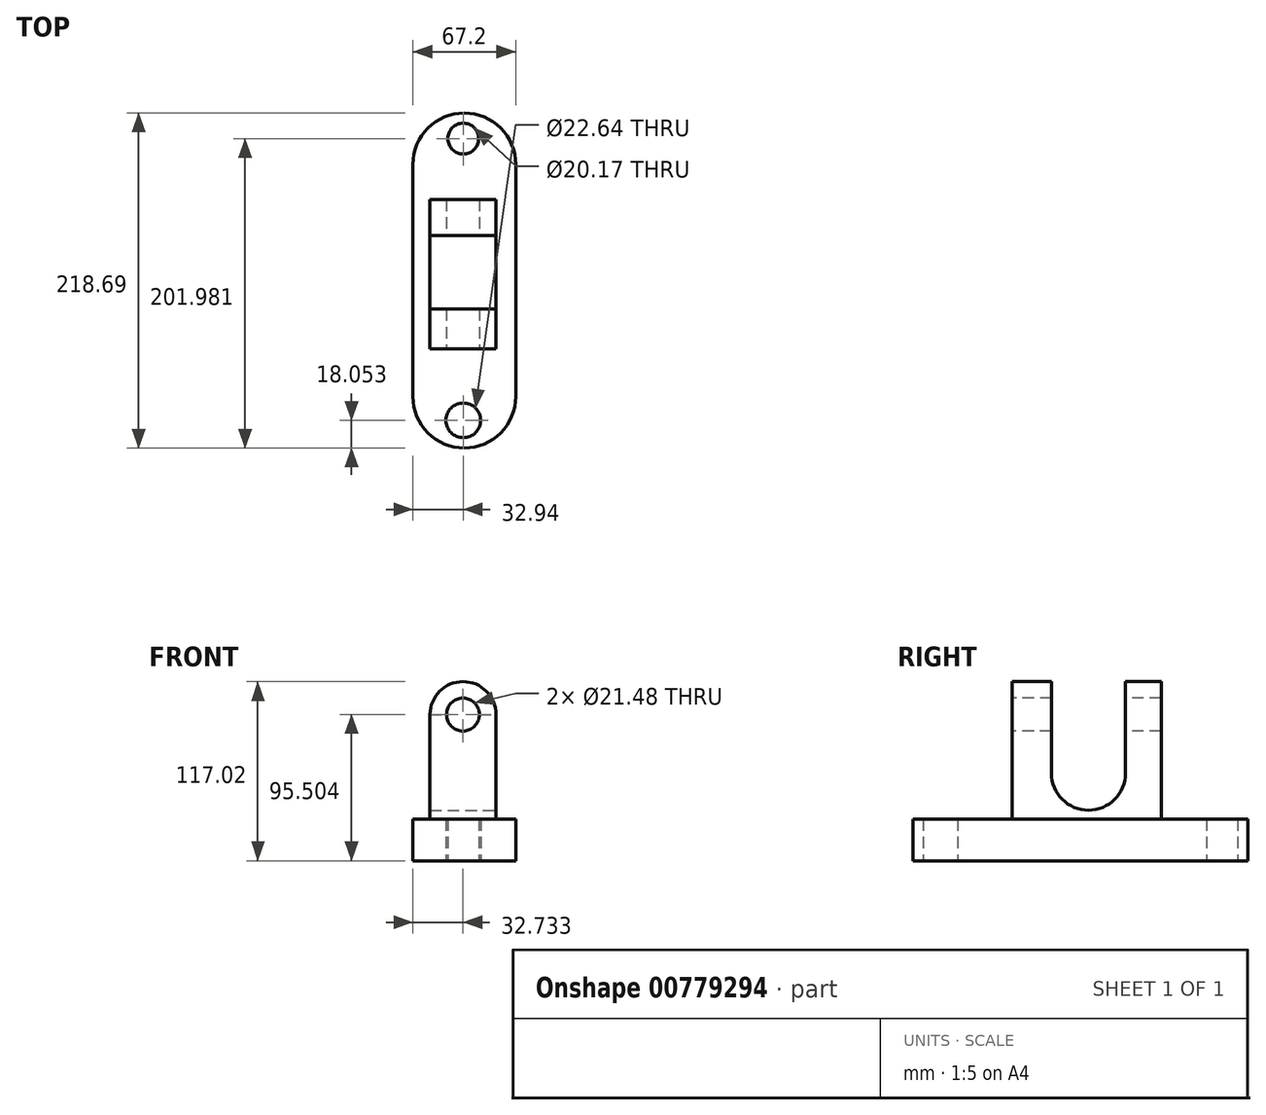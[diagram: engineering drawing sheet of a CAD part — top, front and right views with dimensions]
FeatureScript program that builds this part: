
annotation { "Feature Type Name" : "Feature", "Feature Type Description" : "" }
export const myFeature = defineFeature(function(context is Context, id is Id, definition is map)
    precondition{}
    {
        {
            var Q0;
            Q0=qCreatedBy(makeId("Top.planeOp"),FACE);
            var sketch = newSketch(context, id + "F0", { "sketchPlane" : qUnion([Q0])});
            skLineSegment(sketch, "E0.bottom", {"start": v(-32.94, -75.57) * mm, "end": v(34.26, -75.57) * mm});
            skLineSegment(sketch, "E0.top", {"start": v(-32.94, 75.92) * mm, "end": v(34.26, 75.92) * mm});
            skLineSegment(sketch, "E0.left", {"start": v(-32.94, -75.57) * mm, "end": v(-32.94, 75.92) * mm});
            skLineSegment(sketch, "E0.right", {"start": v(34.26, -75.57) * mm, "end": v(34.26, 75.92) * mm});
            skArc(sketch, "E1", {"start": v(-32.94, -75.57) * mm, "mid": v(0.66, -109.17) * mm, "end": v(34.26, -75.57) * mm});
            skArc(sketch, "E2", {"start": v(34.26, 75.92) * mm, "mid": v(0.66, 109.52) * mm, "end": v(-32.94, 75.92) * mm});
            skCircle(sketch, "E3", {"center": v(0, -91.12) * mm, "radius": 11.32 * mm});
            skCircle(sketch, "E4", {"center": v(0, 92.81) * mm, "radius": 10.08 * mm});
            skSolve(sketch);
        }
        {
            var Q0;
            Q0=makeQuery(id+"F0.imprint","IMPRINT",FACE,{"disambiguationData":[TD([[makeQuery(id+"F0.imprint","IMPRINT",EDGE,{"derivedFrom":sQuery(id+"F0.wireOp",EDGE,"E0.bottom")}),1.0]])]});
            var Q1;
            Q1=makeQuery(id+"F0.imprint","IMPRINT",FACE,{"disambiguationData":[TD([[makeQuery(id+"F0.imprint","IMPRINT",EDGE,{"derivedFrom":sQuery(id+"F0.wireOp",EDGE,"E0.top")}),1.0]])]});
            var Q2;
            Q2=makeQuery(id+"F0.imprint","IMPRINT",FACE,{"disambiguationData":[TD([[makeQuery(id+"F0.imprint","IMPRINT",EDGE,{"derivedFrom":sQuery(id+"F0.wireOp",EDGE,"E0.bottom")}),-1.0]])]});
            extrude(context, id + "F1", {"entities" : qUnion([Q0, Q1, Q2]), "depth" : 27.18 * mm, "offsetDistance" : 25.4 * mm});
        }
        {
            var Q0;
            Q0=makeQuery(id+"F1.opExtrude","CAP_FACE",FACE,{"disambiguationData":[OSD([sQuery(id+"F0.wireOp",EDGE,"E0.left"),sQuery(id+"F0.wireOp",EDGE,"E0.right"),sQuery(id+"F0.wireOp",EDGE,"E1"),sQuery(id+"F0.wireOp",EDGE,"E2"),sQuery(id+"F0.wireOp",EDGE,"E3"),sQuery(id+"F0.wireOp",EDGE,"E4")])],"isStart":false});
            var sketch = newSketch(context, id + "F2", { "sketchPlane" : qUnion([Q0])});
            skLineSegment(sketch, "E5.bottom", {"start": v(-21.73, -44.46) * mm, "end": v(21.31, -44.46) * mm});
            skLineSegment(sketch, "E5.top", {"start": v(-21.73, 53.01) * mm, "end": v(21.31, 53.01) * mm});
            skLineSegment(sketch, "E5.left", {"start": v(-21.73, -44.46) * mm, "end": v(-21.73, 53.01) * mm});
            skLineSegment(sketch, "E5.right", {"start": v(21.31, -44.46) * mm, "end": v(21.31, 53.01) * mm});
            skSolve(sketch);
        }
        {
            var Q0;
            Q0 = qSketchRegion(id + "F2", true);
            extrude(context, id + "F3", {"entities" : qUnion([Q0]), "operationType" : NewBodyOperationType.ADD, "depth" : 68.33 * mm, "offsetDistance" : 25.4 * mm});
        }
        {
            var Q0;
            Q0=makeQuery(id+"F3.opExtrude","SWEPT_FACE",FACE,{"disambiguationData":[OSD([sQuery(id+"F2.wireOp",EDGE,"E5.right")])]});
            var sketch = newSketch(context, id + "F4", { "sketchPlane" : qUnion([Q0])});
            skLineSegment(sketch, "E6.bottom", {"start": v(-18.68, 95.5) * mm, "end": v(29.7, 95.5) * mm});
            skLineSegment(sketch, "E6.top", {"start": v(-18.68, 57.26) * mm, "end": v(29.7, 57.26) * mm});
            skLineSegment(sketch, "E6.left", {"start": v(-18.68, 95.5) * mm, "end": v(-18.68, 57.26) * mm});
            skLineSegment(sketch, "E6.right", {"start": v(29.7, 95.5) * mm, "end": v(29.7, 57.26) * mm});
            skArc(sketch, "E7", {"start": v(-18.68, 57.26) * mm, "mid": v(5.51, 33.07) * mm, "end": v(29.7, 57.26) * mm});
            skSolve(sketch);
        }
        {
            var Q0;
            Q0=makeQuery(id+"F4.imprint","IMPRINT",FACE,{"disambiguationData":[TD([[makeQuery(id+"F4.imprint","IMPRINT",EDGE,{"derivedFrom":sQuery(id+"F4.wireOp",EDGE,"E6.bottom")}),-1.0]])]});
            var Q1;
            Q1=makeQuery(id+"F4.imprint","IMPRINT",FACE,{"disambiguationData":[TD([[makeQuery(id+"F4.imprint","IMPRINT",EDGE,{"derivedFrom":sQuery(id+"F4.wireOp",EDGE,"E6.top")}),-1.0]])]});
            extrude(context, id + "F5", {"entities" : qUnion([Q0, Q1]), "operationType" : NewBodyOperationType.REMOVE, "oppositeDirection" : true, "depth" : 120.9 * mm, "offsetDistance" : 25.4 * mm});
        }
        {
            var Q0;
            Q0=makeQuery(id+"F3.opExtrude","SWEPT_FACE",FACE,{"disambiguationData":[OSD([sQuery(id+"F2.wireOp",EDGE,"E5.top")])]});
            var sketch = newSketch(context, id + "F6", { "sketchPlane" : qUnion([Q0])});
            skArc(sketch, "E8", {"start": v(21.73, 95.5) * mm, "mid": v(0.2, 117.02) * mm, "end": v(-21.31, 95.5) * mm});
            skSolve(sketch);
        }
        {
            var Q0;
            Q0=makeQuery(id+"F6.imprint","IMPRINT",FACE,{"disambiguationData":[TD([[makeQuery(id+"F6.imprint","IMPRINT",EDGE,{"derivedFrom":sQuery(id+"F6.wireOp",EDGE,"E8")}),1.0]])]});
            extrude(context, id + "F7", {"entities" : qUnion([Q0]), "operationType" : NewBodyOperationType.ADD, "oppositeDirection" : true, "depth" : 22.35 * mm, "offsetDistance" : 25.4 * mm});
        }
        {
            var Q0;
            Q0=makeQuery(id+"F7.opExtrude","CAP_FACE",FACE,{"disambiguationData":[OSD([sQuery(id+"F2.wireOp",EDGE,"E5.top"),sQuery(id+"F6.wireOp",EDGE,"E8")])],"isStart":false});
            extrude(context, id + "F8", {"entities" : qUnion([Q0]), "operationType" : NewBodyOperationType.ADD, "depth" : 1.02 * mm, "offsetDistance" : 25.4 * mm});
        }
        {
            var Q0;
            Q0=makeQuery(id+"F3.opExtrude","SWEPT_FACE",FACE,{"disambiguationData":[OSD([sQuery(id+"F2.wireOp",EDGE,"E5.bottom")])]});
            var sketch = newSketch(context, id + "F9", { "sketchPlane" : qUnion([Q0])});
            skArc(sketch, "E9", {"start": v(21.31, 95.5) * mm, "mid": v(-0.2, 117.02) * mm, "end": v(-21.73, 95.5) * mm});
            skSolve(sketch);
        }
        {
            var Q0;
            Q0=makeQuery(id+"F9.imprint","IMPRINT",FACE,{"disambiguationData":[TD([[makeQuery(id+"F9.imprint","IMPRINT",EDGE,{"derivedFrom":sQuery(id+"F9.wireOp",EDGE,"E9")}),1.0]])]});
            extrude(context, id + "F10", {"entities" : qUnion([Q0]), "operationType" : NewBodyOperationType.ADD, "oppositeDirection" : true, "depth" : 25.9 * mm, "offsetDistance" : 25.4 * mm});
        }
        {
            var Q0;
            {var subQ0=sQuery(id+"F2.wireOp",EDGE,"E5.bottom");Q0=makeQuery(id+"F10.boolean.opBoolean","MERGE",FACE,{"derivedFrom":[makeQuery(id+"F3.opExtrude","SWEPT_FACE",FACE,{"disambiguationData":[OSD([subQ0])]}),makeQuery(id+"F10.opExtrude","CAP_FACE",FACE,{"disambiguationData":[OSD([subQ0,sQuery(id+"F9.wireOp",EDGE,"E9")])],"isStart":true})]});}
            var sketch = newSketch(context, id + "F11", { "sketchPlane" : qUnion([Q0])});
            skCircle(sketch, "E10", {"center": v(-0.2, 95.5) * mm, "radius": 10.74 * mm});
            skSolve(sketch);
        }
        {
            var Q0;
            Q0 = qSketchRegion(id + "F11", true);
            extrude(context, id + "F12", {"entities" : qUnion([Q0]), "operationType" : NewBodyOperationType.REMOVE, "oppositeDirection" : true, "depth" : 138.94 * mm, "offsetDistance" : 25.4 * mm});
        }
    });
